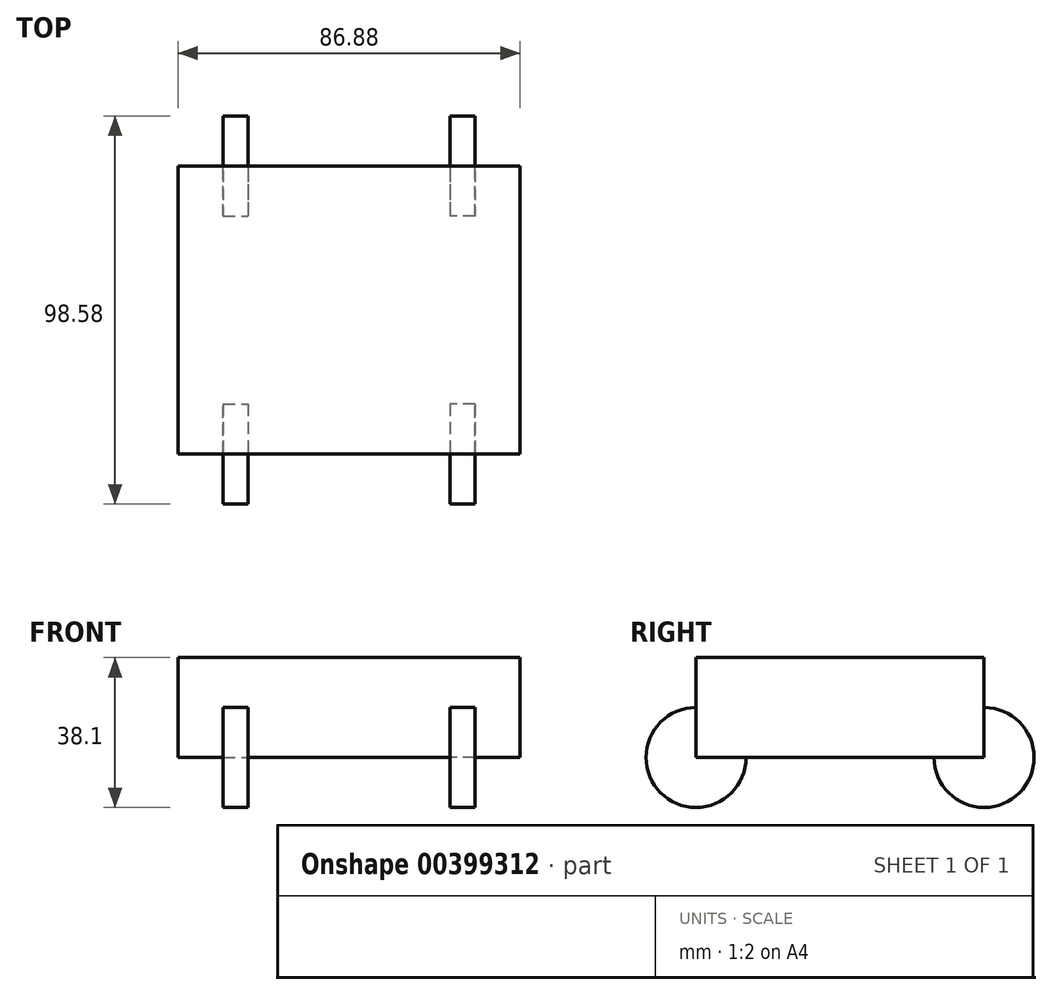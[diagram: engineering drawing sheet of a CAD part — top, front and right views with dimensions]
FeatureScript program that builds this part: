
annotation { "Feature Type Name" : "Feature", "Feature Type Description" : "" }
export const myFeature = defineFeature(function(context is Context, id is Id, definition is map)
    precondition{}
    {
        {
            var Q0;
            Q0=qCreatedBy(makeId("Top.planeOp"),FACE);
            var sketch = newSketch(context, id + "F0", { "sketchPlane" : qUnion([Q0])});
            skLineSegment(sketch, "E0.bottom", {"start": v(-25.63, 23.07) * mm, "end": v(43.44, 23.07) * mm});
            skLineSegment(sketch, "E0.top", {"start": v(-25.63, -50.11) * mm, "end": v(43.44, -50.11) * mm});
            skLineSegment(sketch, "E0.left", {"start": v(-25.63, 23.07) * mm, "end": v(-25.63, -50.11) * mm});
            skLineSegment(sketch, "E0.right", {"start": v(43.44, 23.07) * mm, "end": v(43.44, -50.11) * mm});
            skSolve(sketch);
        }
        {
            var Q0;
            Q0=makeQuery(id+"F0.imprint","IMPRINT",FACE,{"disambiguationData":[TD([[makeQuery(id+"F0.imprint","IMPRINT",EDGE,{"derivedFrom":sQuery(id+"F0.wireOp",EDGE,"E0.bottom")}),-1.0]])]});
            extrude(context, id + "F1", {"entities" : qUnion([Q0]), "depth" : 25.4 * mm, "offsetDistance" : 25.4 * mm});
        }
        {
            var Q0;
            Q0=makeQuery(id+"F1.opExtrude","SWEPT_FACE",FACE,{"disambiguationData":[OSD([sQuery(id+"F0.wireOp",EDGE,"E0.left")])]});
            var sketch = newSketch(context, id + "F2", { "sketchPlane" : qUnion([Q0])});
            skCircle(sketch, "E1", {"center": v(-23.07, 0) * mm, "radius": 12.7 * mm});
            skCircle(sketch, "E2", {"center": v(50.11, 0) * mm, "radius": 12.7 * mm});
            skSolve(sketch);
        }
        {
            var Q0;
            {var subQ0=sQuery(id+"F2.wireOp",EDGE,"E1");var subQ1=sQuery(id+"F0.wireOp",EDGE,"E0.left");var subQ4=makeQuery(id+"F1.opExtrude","CAP_EDGE",EDGE,{"disambiguationData":[OSD([subQ1])],"isStart":true});var subQ5=makeQuery(id+"F2.imprint","INTERSECT",VERTEX,{"derivedFrom":[subQ4,subQ0]});Q0=makeQuery(id+"F2.imprint","IMPRINT",FACE,{"disambiguationData":[TD([[makeQuery(id+"F2.imprint","IMPRINT",EDGE,{"disambiguationData":[TD([[subQ5,1.0]])],"derivedFrom":subQ0}),1.0]])]});}
            var Q1;
            {var subQ0=sQuery(id+"F2.wireOp",EDGE,"E1");var subQ1=sQuery(id+"F0.wireOp",EDGE,"E0.left");var subQ4=makeQuery(id+"F1.opExtrude","CAP_EDGE",EDGE,{"disambiguationData":[OSD([subQ1])],"isStart":true});var subQ5=makeQuery(id+"F2.imprint","INTERSECT",VERTEX,{"derivedFrom":[subQ4,subQ0]});Q1=makeQuery(id+"F2.imprint","IMPRINT",FACE,{"disambiguationData":[TD([[makeQuery(id+"F2.imprint","IMPRINT",EDGE,{"disambiguationData":[TD([[subQ5,-1.0]])],"derivedFrom":subQ0}),1.0]])]});}
            var Q2;
            {var subQ0=sQuery(id+"F2.wireOp",EDGE,"E2");var subQ1=sQuery(id+"F0.wireOp",EDGE,"E0.left");var subQ4=makeQuery(id+"F1.opExtrude","CAP_EDGE",EDGE,{"disambiguationData":[OSD([subQ1])],"isStart":true});var subQ5=makeQuery(id+"F2.imprint","INTERSECT",VERTEX,{"derivedFrom":[subQ4,subQ0]});Q2=makeQuery(id+"F2.imprint","IMPRINT",FACE,{"disambiguationData":[TD([[makeQuery(id+"F2.imprint","IMPRINT",EDGE,{"disambiguationData":[TD([[subQ5,-1.0]])],"derivedFrom":subQ0}),1.0]])]});}
            var Q3;
            {var subQ0=sQuery(id+"F2.wireOp",EDGE,"E2");var subQ1=sQuery(id+"F0.wireOp",EDGE,"E0.left");var subQ4=makeQuery(id+"F1.opExtrude","CAP_EDGE",EDGE,{"disambiguationData":[OSD([subQ1])],"isStart":true});var subQ5=makeQuery(id+"F2.imprint","INTERSECT",VERTEX,{"derivedFrom":[subQ4,subQ0]});Q3=makeQuery(id+"F2.imprint","IMPRINT",FACE,{"disambiguationData":[TD([[makeQuery(id+"F2.imprint","IMPRINT",EDGE,{"disambiguationData":[TD([[subQ5,1.0]])],"derivedFrom":subQ0}),1.0]])]});}
            extrude(context, id + "F3", {"entities" : qUnion([Q0, Q1, Q2, Q3]), "operationType" : NewBodyOperationType.ADD, "depth" : 6.35 * mm, "offsetDistance" : 25.4 * mm});
        }
        {
            var Q0;
            Q0=makeQuery(id+"F1.opExtrude","SWEPT_BODY",BODY,{"disambiguationData":[OSD([sQuery(id+"F0.wireOp",EDGE,"E0.bottom"),sQuery(id+"F0.wireOp",EDGE,"E0.top"),sQuery(id+"F0.wireOp",EDGE,"E0.left"),sQuery(id+"F0.wireOp",EDGE,"E0.right")])]});
            var Q1;
            Q1=qCreatedBy(makeId("Right.planeOp"),FACE);
            mirror(context, id + "F4", {"operationType" : NewBodyOperationType.ADD, "entities" : qUnion([Q0]), "mirrorPlane" : qUnion([Q1])});
        }
    });
